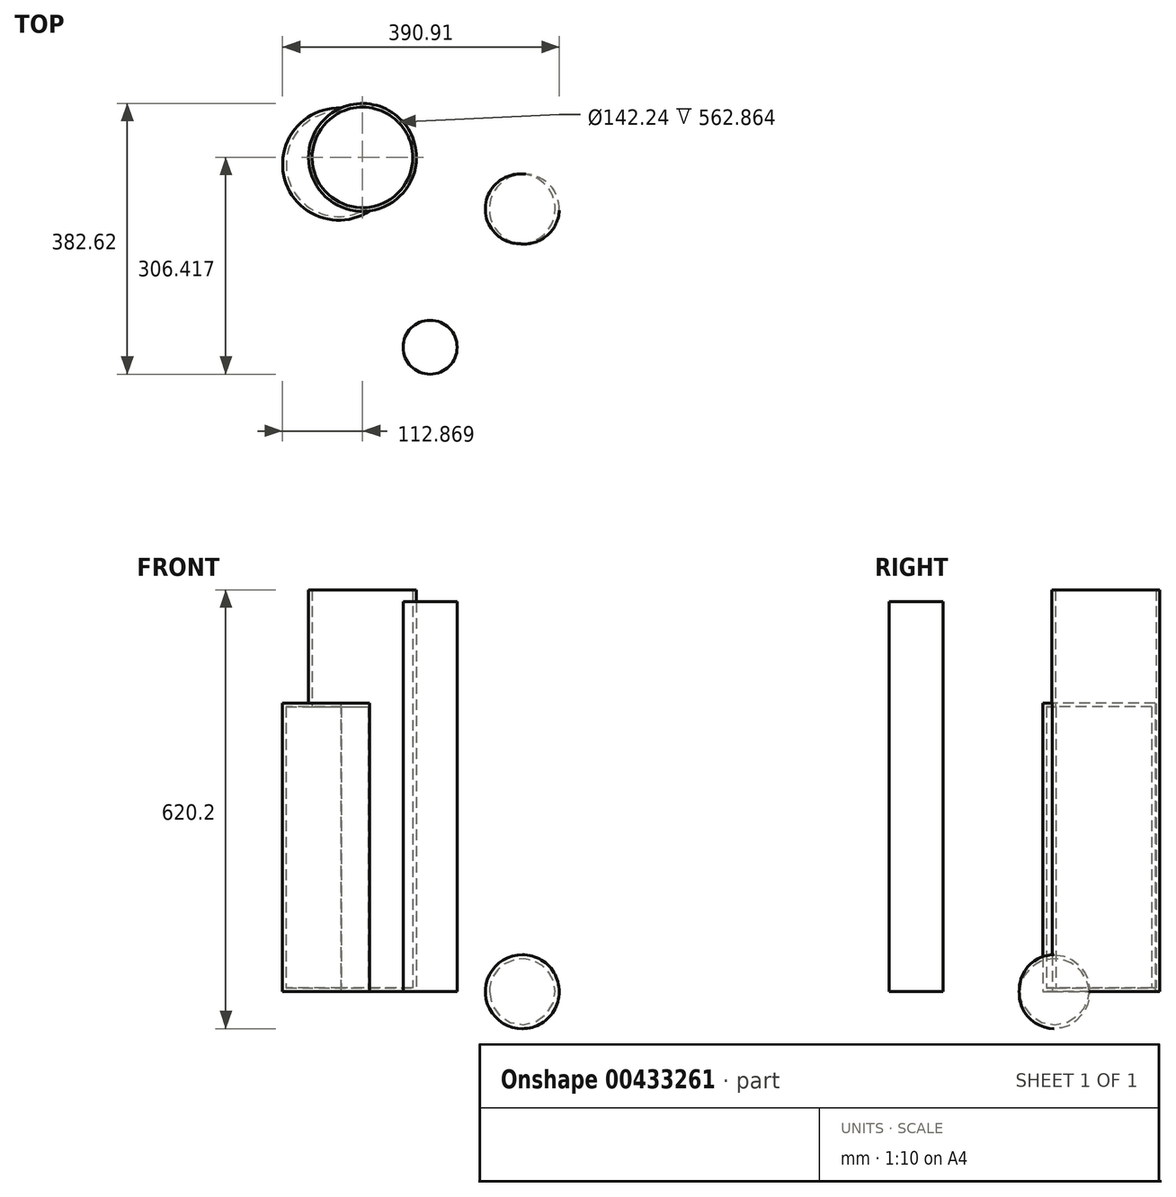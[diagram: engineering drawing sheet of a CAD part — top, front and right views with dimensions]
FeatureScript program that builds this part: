
annotation { "Feature Type Name" : "Feature", "Feature Type Description" : "" }
export const myFeature = defineFeature(function(context is Context, id is Id, definition is map)
    precondition{}
    {
        {
            var Q0;
            Q0=qCreatedBy(makeId("Top.planeOp"),FACE);
            var sketch = newSketch(context, id + "F0", { "sketchPlane" : qUnion([Q0])});
            skCircle(sketch, "E0", {"center": v(-74.76, 26.98) * mm, "radius": 76.2 * mm});
            skSolve(sketch);
        }
        {
            var Q0;
            Q0=qCreatedBy(makeId("Top.planeOp"),FACE);
            var sketch = newSketch(context, id + "F1", { "sketchPlane" : qUnion([Q0])});
            skCircle(sketch, "E1", {"center": v(-108.37, 17.49) * mm, "radius": 79.25 * mm});
            skSolve(sketch);
        }
        {
            var Q0;
            Q0=makeQuery(id+"F0.imprint","IMPRINT",FACE,{"disambiguationData":[TD([[makeQuery(id+"F0.imprint","IMPRINT",EDGE,{"derivedFrom":sQuery(id+"F0.wireOp",EDGE,"E0")}),1.0]])]});
            extrude(context, id + "F2", {"entities" : qUnion([Q0]), "depth" : 567.94 * mm});
        }
        {
            var Q0;
            Q0=makeQuery(id+"F1.imprint","IMPRINT",FACE,{"disambiguationData":[TD([[makeQuery(id+"F1.imprint","IMPRINT",EDGE,{"derivedFrom":sQuery(id+"F1.wireOp",EDGE,"E1")}),1.0]])]});
            extrude(context, id + "F3", {"entities" : qUnion([Q0]), "operationType" : NewBodyOperationType.ADD, "depth" : 407.92 * mm});
        }
        {
            var Q0;
            Q0=makeQuery(id+"F2.opExtrude","CAP_FACE",FACE,{"disambiguationData":[OSD([sQuery(id+"F0.wireOp",EDGE,"E0")])],"isStart":false});
            shell(context, id + "F4", {"entities" : qUnion([Q0]), "thickness" : 5.08 * mm});
        }
        {
            var Q0;
            Q0=qCreatedBy(makeId("Top.planeOp"),FACE);
            var sketch = newSketch(context, id + "F5", { "sketchPlane" : qUnion([Q0])});
            skCircle(sketch, "E2", {"center": v(20.86, -241.34) * mm, "radius": 38.1 * mm});
            skSolve(sketch);
        }
        {
            var Q0;
            Q0=makeQuery(id+"F5.imprint","IMPRINT",FACE,{"disambiguationData":[TD([[makeQuery(id+"F5.imprint","IMPRINT",EDGE,{"derivedFrom":sQuery(id+"F5.wireOp",EDGE,"E2")}),1.0]])]});
            extrude(context, id + "F6", {"entities" : qUnion([Q0]), "depth" : 551.18 * mm});
        }
        {
            var Q0;
            Q0=qCreatedBy(makeId("Top.planeOp"),FACE);
            var sketch = newSketch(context, id + "F7", { "sketchPlane" : qUnion([Q0])});
            skCircle(sketch, "E3", {"center": v(153.9, -46) * mm, "radius": 49.38 * mm});
            skLineSegment(sketch, "E4", {"start": v(148.63, -140.62) * mm, "end": v(148.63, -108.84) * mm});
            skLineSegment(sketch, "E5", {"start": v(148.63, -108.84) * mm, "end": v(153.9, 29.89) * mm});
            skSolve(sketch);
        }
        {
            var Q0;
            {var subQ0=sQuery(id+"F7.wireOp",EDGE,"E5");var subQ1=sQuery(id+"F7.wireOp",EDGE,"E3");var subQ2=makeQuery(id+"F7.imprint","INTERSECT",VERTEX,{"disambiguationData":[OD(0.0)],"derivedFrom":[subQ1,subQ0]});Q0=makeQuery(id+"F7.imprint","IMPRINT",FACE,{"disambiguationData":[TD([[makeQuery(id+"F7.imprint","IMPRINT",EDGE,{"disambiguationData":[TD([[subQ2,-1.0]])],"derivedFrom":subQ1}),1.0]])]});}
            var Q1;
            Q1=sQuery(id+"F7.wireOp",EDGE,"E5");
            revolve(context, id + "F8", {"entities" : qUnion([Q0]), "axis" : qUnion([Q1]), "revolveType" : RevolveType.FULL});
        }
    });
